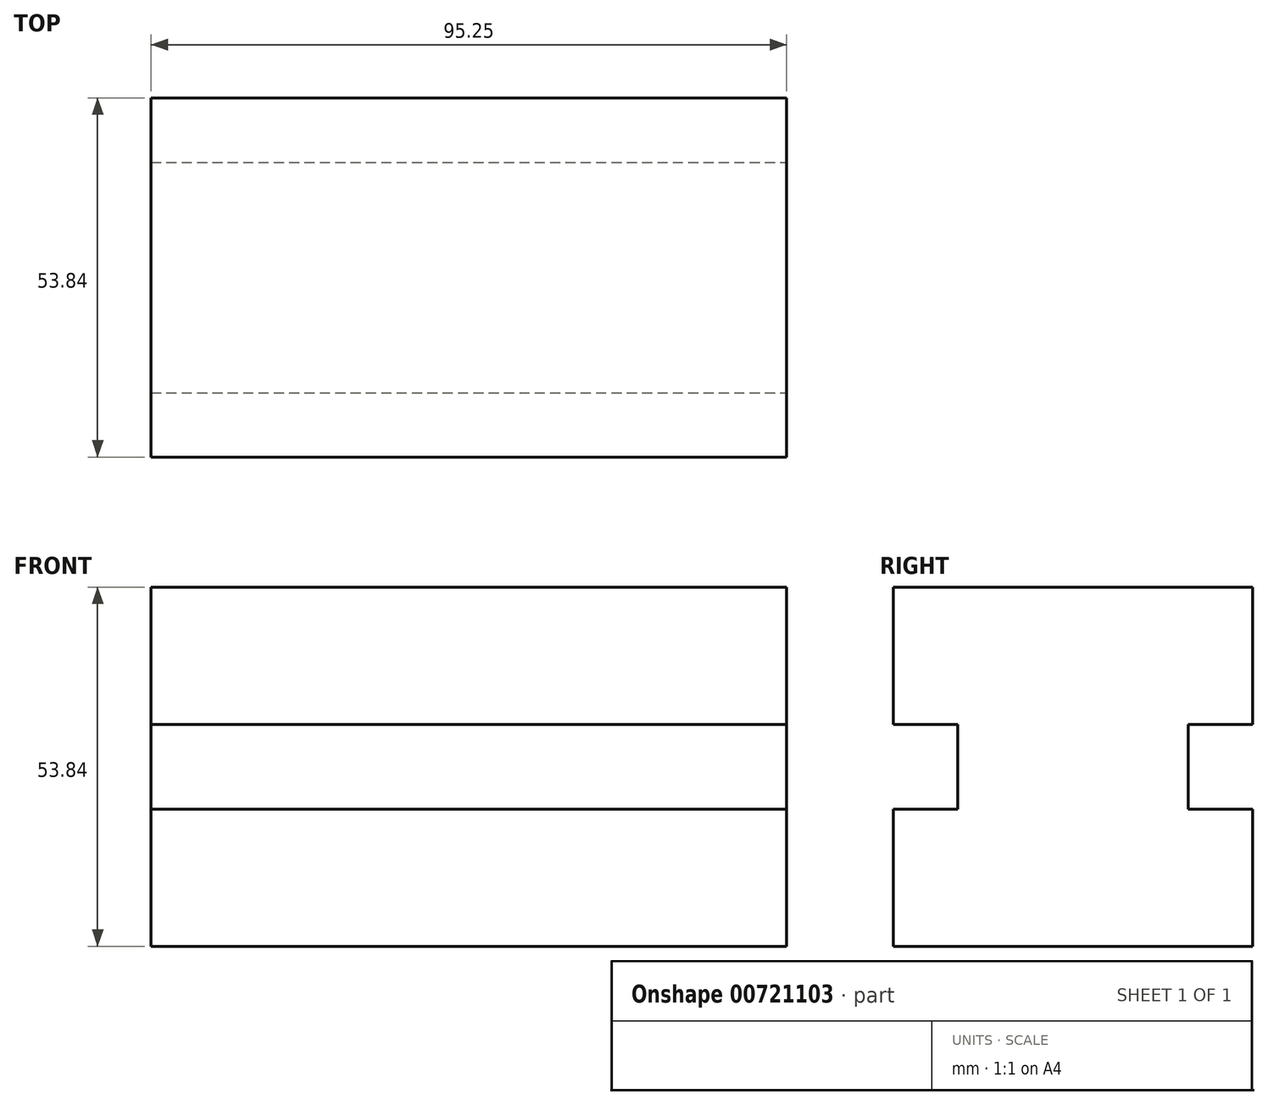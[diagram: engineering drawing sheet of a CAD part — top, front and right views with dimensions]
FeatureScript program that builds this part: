
annotation { "Feature Type Name" : "Feature", "Feature Type Description" : "" }
export const myFeature = defineFeature(function(context is Context, id is Id, definition is map)
    precondition{}
    {
        {
            var Q0;
            Q0=qCreatedBy(makeId("Right.planeOp"),FACE);
            var sketch = newSketch(context, id + "F0", { "sketchPlane" : qUnion([Q0])});
            skLineSegment(sketch, "E0.bottom", {"start": v(26.92, -26.92) * mm, "end": v(-26.92, -26.92) * mm});
            skLineSegment(sketch, "E0.top", {"start": v(26.92, 26.92) * mm, "end": v(-26.92, 26.92) * mm});
            skLineSegment(sketch, "E0.left", {"start": v(26.92, -26.92) * mm, "end": v(26.92, -6.35) * mm});
            skLineSegment(sketch, "E0.right", {"start": v(-26.92, -26.92) * mm, "end": v(-26.92, -6.35) * mm});
            skPoint(sketch, "E0.middle", {"position": v(0, 0) * mm});
            skLineSegment(sketch, "E1.bottom", {"start": v(-26.92, -6.35) * mm, "end": v(-17.27, -6.35) * mm});
            skLineSegment(sketch, "E1.top", {"start": v(-26.92, 6.35) * mm, "end": v(-17.27, 6.35) * mm});
            skLineSegment(sketch, "E1.right", {"start": v(-17.27, -6.35) * mm, "end": v(-17.27, 6.35) * mm});
            skLineSegment(sketch, "E2", {"start": v(0, 33.86) * mm, "end": v(0, -45.43) * mm, "construction": true});
            skLineSegment(sketch, "E3.MirrorCS", {"start": v(26.92, 6.35) * mm, "end": v(17.27, 6.35) * mm});
            skLineSegment(sketch, "E4.MirrorCS", {"start": v(17.27, -6.35) * mm, "end": v(17.27, 6.35) * mm});
            skLineSegment(sketch, "E5.MirrorCS", {"start": v(26.92, -6.35) * mm, "end": v(17.27, -6.35) * mm});
            skLineSegment(sketch, "E6.trimOffspring", {"start": v(-26.92, 6.35) * mm, "end": v(-26.92, 26.92) * mm});
            skLineSegment(sketch, "E7.trimOffspring", {"start": v(26.92, 6.35) * mm, "end": v(26.92, 26.92) * mm});
            skSolve(sketch);
        }
        {
            var Q0;
            Q0=makeQuery(id+"F0.imprint","IMPRINT",FACE,{"disambiguationData":[TD([[makeQuery(id+"F0.imprint","IMPRINT",EDGE,{"derivedFrom":sQuery(id+"F0.wireOp",EDGE,"E0.bottom")}),-1.0]])]});
            extrude(context, id + "F1", {"entities" : qUnion([Q0]), "oppositeDirection" : true, "depth" : 95.25 * mm, "offsetDistance" : 25.4 * mm});
        }
    });
